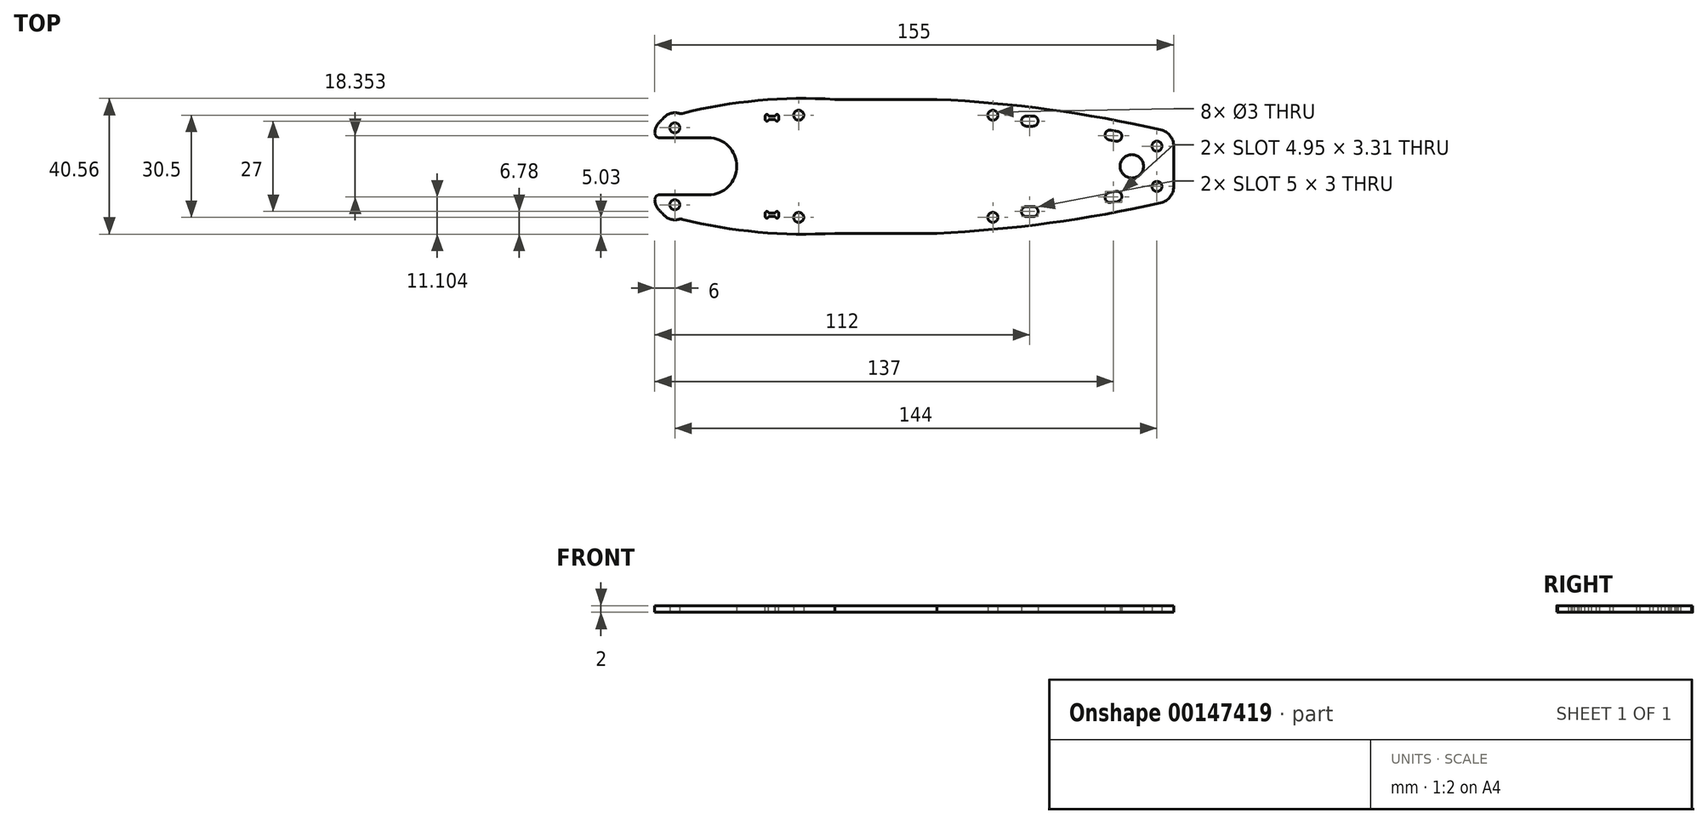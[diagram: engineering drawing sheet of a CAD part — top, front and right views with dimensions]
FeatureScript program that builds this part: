
annotation { "Feature Type Name" : "Feature", "Feature Type Description" : "" }
export const myFeature = defineFeature(function(context is Context, id is Id, definition is map)
    precondition{}
    {
        {
            var Q0;
            Q0=qCreatedBy(makeId("Top.planeOp"),FACE);
            var sketch = newSketch(context, id + "F0", { "sketchPlane" : qUnion([Q0])});
            skLineSegment(sketch, "E0", {"start": v(-44.5, 0) * mm, "end": v(86, 0) * mm, "construction": true});
            skLineSegment(sketch, "E1", {"start": v(-69, 9.77) * mm, "end": v(-69, 10) * mm});
            skLineSegment(sketch, "E2", {"start": v(-15.25, 20) * mm, "end": v(15.25, 20) * mm});
            skLineSegment(sketch, "E3", {"start": v(86, 0) * mm, "end": v(86, 6.03) * mm});
            skArc(sketch, "E4", {"start": v(-15.25, 20) * mm, "mid": v(-38.16, 19.65) * mm, "end": v(-60.74, 15.81) * mm});
            skArc(sketch, "E5", {"start": v(82.11, 10.9) * mm, "mid": v(48.88, 16.94) * mm, "end": v(15.25, 20) * mm});
            skPoint(sketch, "E6.visualSharp", {"position": v(-69, 13.5) * mm});
            skArc(sketch, "E6.filletArc", {"start": v(-67.03, 13.75) * mm, "mid": v(-68.48, 11.99) * mm, "end": v(-69, 9.77) * mm});
            skPoint(sketch, "E7.visualSharp", {"position": v(86, 10) * mm});
            skArc(sketch, "E7.filletArc", {"start": v(86, 6.03) * mm, "mid": v(84.9, 9.15) * mm, "end": v(82.11, 10.9) * mm});
            skCircle(sketch, "E8", {"center": v(-26, 15.25) * mm, "radius": 1.5 * mm});
            skCircle(sketch, "E9", {"center": v(32, 15.25) * mm, "radius": 1.5 * mm});
            skLineSegment(sketch, "E10.bottom", {"start": v(67.26, 10.83) * mm, "end": v(69.26, 10.48) * mm});
            skLineSegment(sketch, "E10.top", {"start": v(66.74, 7.88) * mm, "end": v(68.74, 7.52) * mm});
            skArc(sketch, "E11", {"start": v(67.26, 10.83) * mm, "mid": v(65.52, 9.61) * mm, "end": v(66.74, 7.88) * mm});
            skArc(sketch, "E12", {"start": v(68.74, 7.52) * mm, "mid": v(70.48, 8.74) * mm, "end": v(69.26, 10.48) * mm});
            skLineSegment(sketch, "E13.bottom", {"start": v(42, 15) * mm, "end": v(44, 15) * mm});
            skLineSegment(sketch, "E13.top", {"start": v(42, 12) * mm, "end": v(44, 12) * mm});
            skArc(sketch, "E14", {"start": v(44, 12) * mm, "mid": v(45.5, 13.5) * mm, "end": v(44, 15) * mm});
            skArc(sketch, "E15", {"start": v(42, 15) * mm, "mid": v(40.5, 13.5) * mm, "end": v(42, 12) * mm});
            skLineSegment(sketch, "E16.bottom", {"start": v(-67.5, 8.5) * mm, "end": v(-53, 8.5) * mm});
            skPoint(sketch, "E17.orphan", {"position": v(-69, 0) * mm});
            skArc(sketch, "E18", {"start": v(-44.5, 0) * mm, "mid": v(-46.99, 6.01) * mm, "end": v(-53, 8.5) * mm});
            skCircle(sketch, "E19", {"center": v(-63, 11.5) * mm, "radius": 1.5 * mm});
            skPoint(sketch, "E20.visualSharp", {"position": v(-69, 8.5) * mm});
            skArc(sketch, "E20.filletArc", {"start": v(-69, 10) * mm, "mid": v(-68.56, 8.94) * mm, "end": v(-67.5, 8.5) * mm});
            skLineSegment(sketch, "E21", {"start": v(67.26, 10.83) * mm, "end": v(67, 9.35) * mm, "construction": true});
            skLineSegment(sketch, "E22", {"start": v(69.26, 10.48) * mm, "end": v(69, 9) * mm, "construction": true});
            skArc(sketch, "E23.MirrorCS", {"start": v(68.74, -7.52) * mm, "mid": v(70.48, -8.74) * mm, "end": v(69.26, -10.48) * mm});
            skLineSegment(sketch, "E24.MirrorCS", {"start": v(67.26, -10.83) * mm, "end": v(69.26, -10.48) * mm});
            skLineSegment(sketch, "E25.MirrorCS", {"start": v(67.26, -10.83) * mm, "end": v(67, -9.35) * mm, "construction": true});
            skLineSegment(sketch, "E26.MirrorCS", {"start": v(69.26, -10.48) * mm, "end": v(69, -9) * mm, "construction": true});
            skArc(sketch, "E27.MirrorCS", {"start": v(-69, -10) * mm, "mid": v(-68.56, -8.94) * mm, "end": v(-67.5, -8.5) * mm});
            skLineSegment(sketch, "E28.MirrorCS", {"start": v(-69, -9.77) * mm, "end": v(-69, -10) * mm});
            skLineSegment(sketch, "E29.MirrorCS", {"start": v(66.74, -7.88) * mm, "end": v(68.74, -7.52) * mm});
            skArc(sketch, "E30.MirrorCS", {"start": v(44, -12) * mm, "mid": v(45.5, -13.5) * mm, "end": v(44, -15) * mm});
            skArc(sketch, "E31.MirrorCS", {"start": v(67.26, -10.83) * mm, "mid": v(65.52, -9.61) * mm, "end": v(66.74, -7.88) * mm});
            skLineSegment(sketch, "E32.MirrorCS", {"start": v(42, -15) * mm, "end": v(44, -15) * mm});
            skLineSegment(sketch, "E33.MirrorCS", {"start": v(42, -12) * mm, "end": v(44, -12) * mm});
            skArc(sketch, "E34.MirrorCS", {"start": v(42, -15) * mm, "mid": v(40.5, -13.5) * mm, "end": v(42, -12) * mm});
            skLineSegment(sketch, "E35.MirrorCS", {"start": v(-67.5, -8.5) * mm, "end": v(-53, -8.5) * mm});
            skArc(sketch, "E36.MirrorCS", {"start": v(86, -6.03) * mm, "mid": v(84.9, -9.15) * mm, "end": v(82.11, -10.9) * mm});
            skCircle(sketch, "E37.MirrorC", {"center": v(-26, -15.25) * mm, "radius": 1.5 * mm});
            skArc(sketch, "E38.MirrorCS", {"start": v(-67.03, -13.75) * mm, "mid": v(-68.48, -11.99) * mm, "end": v(-69, -9.77) * mm});
            skCircle(sketch, "E39.MirrorC", {"center": v(-63, -11.5) * mm, "radius": 1.5 * mm});
            skCircle(sketch, "E40.MirrorC", {"center": v(32, -15.25) * mm, "radius": 1.5 * mm});
            skPoint(sketch, "E41.MirrorP", {"position": v(-69, -8.5) * mm});
            skPoint(sketch, "E42.MirrorP", {"position": v(-69, -13.5) * mm});
            skArc(sketch, "E43.MirrorCS", {"start": v(-44.5, 0) * mm, "mid": v(-46.99, -6.01) * mm, "end": v(-53, -8.5) * mm});
            skArc(sketch, "E44.MirrorCS", {"start": v(-15.25, -20) * mm, "mid": v(-38.16, -19.65) * mm, "end": v(-60.74, -15.81) * mm});
            skArc(sketch, "E45.MirrorCS", {"start": v(82.11, -10.9) * mm, "mid": v(48.88, -16.94) * mm, "end": v(15.25, -20) * mm});
            skLineSegment(sketch, "E46.MirrorCS", {"start": v(-15.25, -20) * mm, "end": v(15.25, -20) * mm});
            skPoint(sketch, "E47.MirrorP", {"position": v(86, -10) * mm});
            skLineSegment(sketch, "E48.MirrorCS", {"start": v(86, 0) * mm, "end": v(86, -6.03) * mm});
            skCircle(sketch, "E49", {"center": v(73.5, 0) * mm, "radius": 3.5 * mm});
            skArc(sketch, "E50", {"start": v(-61.77, 15.83) * mm, "mid": v(-64.47, 15.75) * mm, "end": v(-66.63, 14.15) * mm});
            skPoint(sketch, "E51.orphan", {"position": v(-65.37, 14.58) * mm});
            skPoint(sketch, "E52.visualSharp", {"position": v(-61.31, 15.67) * mm});
            skArc(sketch, "E52.filletArc", {"start": v(-61.77, 15.83) * mm, "mid": v(-61.26, 15.75) * mm, "end": v(-60.74, 15.81) * mm});
            skPoint(sketch, "E53.visualSharp", {"position": v(-66.8, 13.92) * mm});
            skArc(sketch, "E53.filletArc", {"start": v(-67.03, 13.75) * mm, "mid": v(-66.82, 13.94) * mm, "end": v(-66.63, 14.15) * mm});
            skArc(sketch, "E54", {"start": v(-66.63, -14.15) * mm, "mid": v(-64.47, -15.75) * mm, "end": v(-61.77, -15.83) * mm});
            skPoint(sketch, "E55.orphan", {"position": v(-65.37, -14.58) * mm});
            skPoint(sketch, "E56.visualSharp", {"position": v(-66.8, -13.92) * mm});
            skArc(sketch, "E56.filletArc", {"start": v(-66.63, -14.15) * mm, "mid": v(-66.82, -13.94) * mm, "end": v(-67.03, -13.75) * mm});
            skPoint(sketch, "E57.visualSharp", {"position": v(-61.31, -15.67) * mm});
            skArc(sketch, "E57.filletArc", {"start": v(-60.74, -15.81) * mm, "mid": v(-61.26, -15.75) * mm, "end": v(-61.77, -15.83) * mm});
            skCircle(sketch, "E58", {"center": v(81, 6) * mm, "radius": 1.5 * mm});
            skCircle(sketch, "E59", {"center": v(81, -6) * mm, "radius": 1.5 * mm});
            skLineSegment(sketch, "E60", {"start": v(81, 6.03) * mm, "end": v(81, 6) * mm, "construction": true});
            skLineSegment(sketch, "E61", {"start": v(81, -6) * mm, "end": v(81, -6.03) * mm, "construction": true});
            skSolve(sketch);
        }
        {
            var Q0;
            Q0=makeQuery(id+"F0.imprint","IMPRINT",FACE,{"disambiguationData":[TD([[makeQuery(id+"F0.imprint","IMPRINT",EDGE,{"derivedFrom":sQuery(id+"F0.wireOp",EDGE,"E2")}),-1.0]])]});
            extrude(context, id + "F1", {"entities" : qUnion([Q0]), "depth" : 2 * mm});
        }
        {
            var Q0;
            Q0=makeQuery(id+"F1.opExtrude","CAP_FACE",FACE,{"disambiguationData":[OSD([sQuery(id+"F0.wireOp",EDGE,"E2"),sQuery(id+"F0.wireOp",EDGE,"E3"),sQuery(id+"F0.wireOp",EDGE,"E4"),sQuery(id+"F0.wireOp",EDGE,"E5"),sQuery(id+"F0.wireOp",EDGE,"E6.filletArc"),sQuery(id+"F0.wireOp",EDGE,"E7.filletArc"),sQuery(id+"F0.wireOp",EDGE,"E8"),sQuery(id+"F0.wireOp",EDGE,"E9"),sQuery(id+"F0.wireOp",EDGE,"qYgZW7lB-CMnV-piOl-7c3a-DXn0YMV1QPsr"),sQuery(id+"F0.wireOp",EDGE,"E10.bottom"),sQuery(id+"F0.wireOp",EDGE,"E10.top"),sQuery(id+"F0.wireOp",EDGE,"E11"),sQuery(id+"F0.wireOp",EDGE,"E12"),sQuery(id+"F0.wireOp",EDGE,"E13.bottom"),sQuery(id+"F0.wireOp",EDGE,"E13.top"),sQuery(id+"F0.wireOp",EDGE,"E14"),sQuery(id+"F0.wireOp",EDGE,"E15"),sQuery(id+"F0.wireOp",EDGE,"E16.bottom"),sQuery(id+"F0.wireOp",EDGE,"E18"),sQuery(id+"F0.wireOp",EDGE,"E19"),sQuery(id+"F0.wireOp",EDGE,"E20.filletArc"),sQuery(id+"F0.wireOp",EDGE,"0b4e915d-b4a6-4427-af53-a3d2afabc14c0.MirrorC"),sQuery(id+"F0.wireOp",EDGE,"E23.MirrorCS"),sQuery(id+"F0.wireOp",EDGE,"E24.MirrorCS"),sQuery(id+"F0.wireOp",EDGE,"E27.MirrorCS"),sQuery(id+"F0.wireOp",EDGE,"E29.MirrorCS"),sQuery(id+"F0.wireOp",EDGE,"E30.MirrorCS"),sQuery(id+"F0.wireOp",EDGE,"E31.MirrorCS"),sQuery(id+"F0.wireOp",EDGE,"E32.MirrorCS"),sQuery(id+"F0.wireOp",EDGE,"E33.MirrorCS"),sQuery(id+"F0.wireOp",EDGE,"E34.MirrorCS"),sQuery(id+"F0.wireOp",EDGE,"E35.MirrorCS"),sQuery(id+"F0.wireOp",EDGE,"E36.MirrorCS"),sQuery(id+"F0.wireOp",EDGE,"E37.MirrorC"),sQuery(id+"F0.wireOp",EDGE,"E38.MirrorCS"),sQuery(id+"F0.wireOp",EDGE,"E39.MirrorC"),sQuery(id+"F0.wireOp",EDGE,"E40.MirrorC"),sQuery(id+"F0.wireOp",EDGE,"E43.MirrorCS"),sQuery(id+"F0.wireOp",EDGE,"E44.MirrorCS"),sQuery(id+"F0.wireOp",EDGE,"E45.MirrorCS"),sQuery(id+"F0.wireOp",EDGE,"E46.MirrorCS"),sQuery(id+"F0.wireOp",EDGE,"E48.MirrorCS"),sQuery(id+"F0.wireOp",EDGE,"E49"),sQuery(id+"F0.wireOp",EDGE,"E50"),sQuery(id+"F0.wireOp",EDGE,"E52.filletArc"),sQuery(id+"F0.wireOp",EDGE,"E53.filletArc"),sQuery(id+"F0.wireOp",EDGE,"E54"),sQuery(id+"F0.wireOp",EDGE,"E56.filletArc"),sQuery(id+"F0.wireOp",EDGE,"E57.filletArc")])],"isStart":false});
            var sketch = newSketch(context, id + "F2", { "sketchPlane" : qUnion([Q0])});
            skLineSegment(sketch, "E62.bottom", {"start": v(-35, 15) * mm, "end": v(-33, 15) * mm});
            skLineSegment(sketch, "E62.top", {"start": v(-35, 14) * mm, "end": v(-33, 14) * mm});
            skLineSegment(sketch, "E63.left", {"start": v(-36, 15) * mm, "end": v(-36, 14) * mm});
            skLineSegment(sketch, "E64.left", {"start": v(-32, 15) * mm, "end": v(-32, 14) * mm});
            skArc(sketch, "E65", {"start": v(-35, 15) * mm, "mid": v(-35.5, 15.5) * mm, "end": v(-36, 15) * mm});
            skArc(sketch, "E66", {"start": v(-32, 15) * mm, "mid": v(-32.5, 15.5) * mm, "end": v(-33, 15) * mm});
            skArc(sketch, "E67", {"start": v(-33, 14) * mm, "mid": v(-32.5, 13.5) * mm, "end": v(-32, 14) * mm});
            skArc(sketch, "E68", {"start": v(-36, 14) * mm, "mid": v(-35.5, 13.5) * mm, "end": v(-35, 14) * mm});
            skArc(sketch, "E69.0.1.0", {"start": v(-36, -15) * mm, "mid": v(-35.5, -15.5) * mm, "end": v(-35, -15) * mm});
            skArc(sketch, "E69.0.1.1", {"start": v(-33, -15) * mm, "mid": v(-32.5, -15.5) * mm, "end": v(-32, -15) * mm});
            skArc(sketch, "E69.0.1.2", {"start": v(-35, -14) * mm, "mid": v(-35.5, -13.5) * mm, "end": v(-36, -14) * mm});
            skArc(sketch, "E69.0.1.3", {"start": v(-32, -14) * mm, "mid": v(-32.5, -13.5) * mm, "end": v(-33, -14) * mm});
            skLineSegment(sketch, "E69.0.1.4", {"start": v(-36, -14) * mm, "end": v(-36, -15) * mm});
            skLineSegment(sketch, "E69.0.1.5", {"start": v(-32, -14) * mm, "end": v(-32, -15) * mm});
            skLineSegment(sketch, "E69.0.1.6", {"start": v(-35, -14) * mm, "end": v(-33, -14) * mm});
            skLineSegment(sketch, "E69.0.1.7", {"start": v(-35, -15) * mm, "end": v(-33, -15) * mm});
            skLineSegment(sketch, "E69.direction1", {"start": v(-36, 14) * mm, "end": v(-12.35, 14) * mm, "construction": true});
            skLineSegment(sketch, "E69.direction2", {"start": v(-36, 14) * mm, "end": v(-36, -15) * mm, "construction": true});
            skSolve(sketch);
        }
        {
            var Q0;
            Q0=qSketchRegion(id+"F2",true);
            extrude(context, id + "F3", {"entities" : qUnion([Q0]), "operationType" : NewBodyOperationType.REMOVE, "oppositeDirection" : true, "depth" : 25 * mm});
        }
    });
